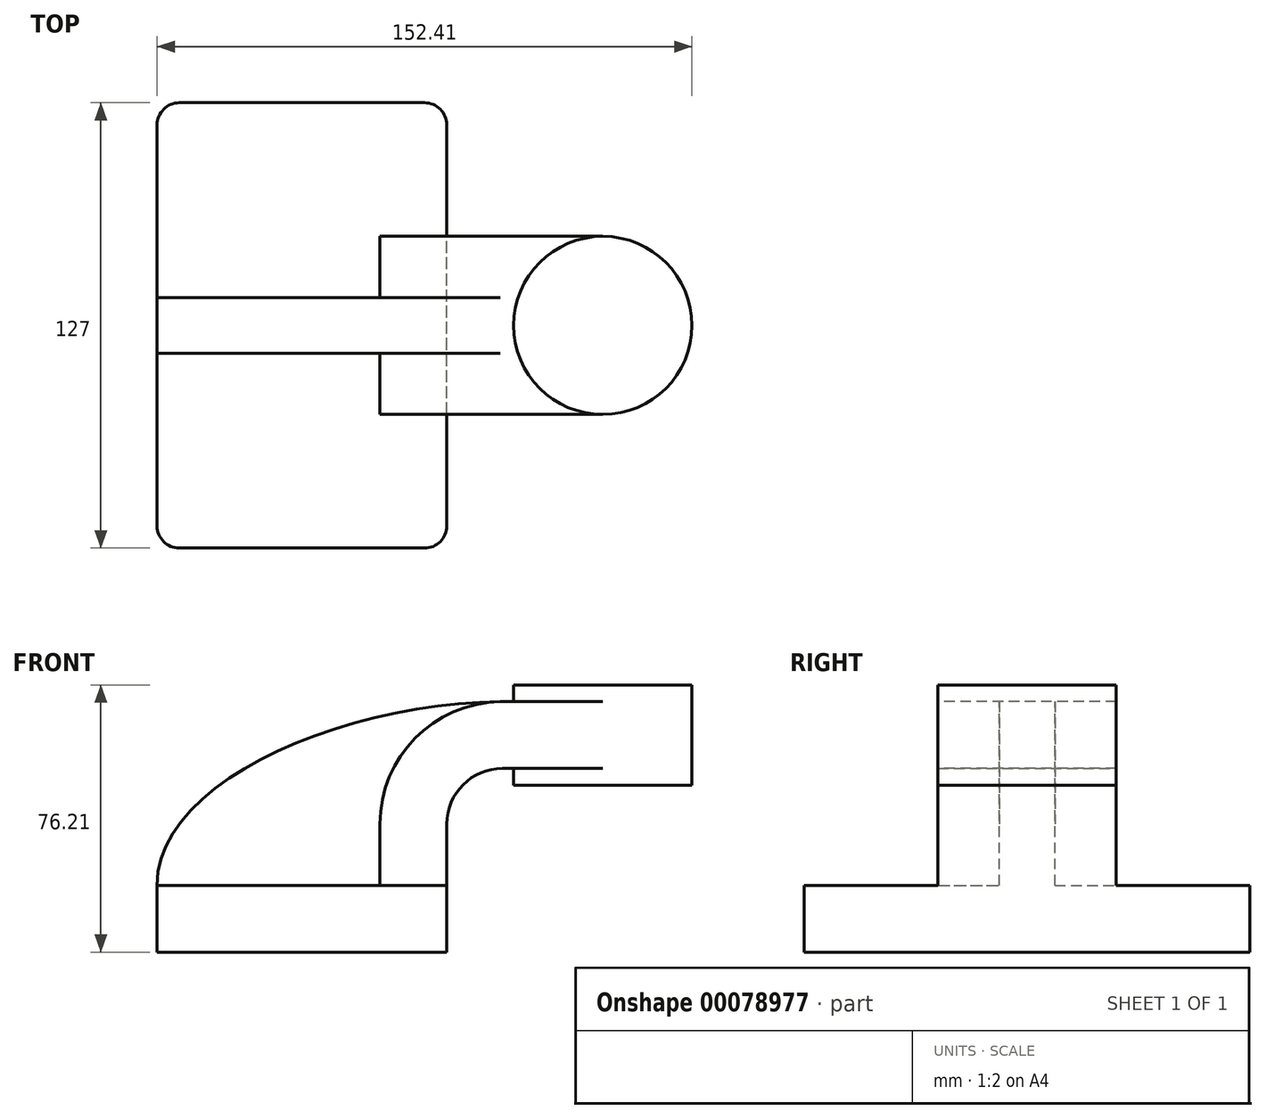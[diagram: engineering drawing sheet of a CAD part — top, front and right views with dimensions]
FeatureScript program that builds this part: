
annotation { "Feature Type Name" : "Feature", "Feature Type Description" : "" }
export const myFeature = defineFeature(function(context is Context, id is Id, definition is map)
    precondition{}
    {
        {
            var Q0;
            Q0=qCreatedBy(makeId("Front.planeOp"),FACE);
            var sketch = newSketch(context, id + "F0", { "sketchPlane" : qUnion([Q0])});
            skLineSegment(sketch, "E0.bottom", {"start": v(41.28, -9.53) * mm, "end": v(-41.27, -9.53) * mm});
            skLineSegment(sketch, "E0.top", {"start": v(41.28, 9.52) * mm, "end": v(-41.28, 9.52) * mm});
            skLineSegment(sketch, "E0.left", {"start": v(41.28, -9.53) * mm, "end": v(41.27, 9.52) * mm});
            skLineSegment(sketch, "E0.right", {"start": v(-41.27, -9.53) * mm, "end": v(-41.28, 9.52) * mm});
            skPoint(sketch, "E0.middle", {"position": v(0, 0) * mm});
            skLineSegment(sketch, "E1.bottom", {"start": v(111.12, 38.1) * mm, "end": v(60.33, 38.1) * mm});
            skLineSegment(sketch, "E1.top", {"start": v(111.12, 66.67) * mm, "end": v(60.33, 66.67) * mm});
            skLineSegment(sketch, "E1.left", {"start": v(111.12, 38.1) * mm, "end": v(111.12, 66.68) * mm});
            skLineSegment(sketch, "E1.right", {"start": v(60.33, 38.1) * mm, "end": v(60.33, 66.67) * mm});
            skPoint(sketch, "E1.middle", {"position": v(85.72, 52.39) * mm});
            skLineSegment(sketch, "E2", {"start": v(41.28, 9.52) * mm, "end": v(41.27, 26.99) * mm});
            skArc(sketch, "E3", {"start": v(41.27, 26.99) * mm, "mid": v(45.92, 38.21) * mm, "end": v(57.15, 42.86) * mm});
            skLineSegment(sketch, "E4", {"start": v(57.15, 42.86) * mm, "end": v(85.72, 42.86) * mm});
            skLineSegment(sketch, "E5.0", {"start": v(57.15, 61.91) * mm, "end": v(85.72, 61.91) * mm});
            skArc(sketch, "E5.1", {"start": v(22.22, 26.99) * mm, "mid": v(32.45, 51.68) * mm, "end": v(57.15, 61.91) * mm});
            skLineSegment(sketch, "E5.2", {"start": v(22.22, 9.52) * mm, "end": v(22.22, 26.99) * mm});
            skFitSpline(sketch, "E6", {"points": [v(-41.28, 9.52) * mm, v(57.15, 61.91) * mm], "startDerivative": vector(-0.62, 89.26) * mm, "endDerivative": vector(135.37, 0.89) * mm});
            skLineSegment(sketch, "E7", {"start": v(85.72, 66.68) * mm, "end": v(85.72, 38.1) * mm});
            skSolve(sketch);
        }
        {
            var Q0;
            Q0=makeQuery(id+"F0.imprint","IMPRINT",FACE,{"disambiguationData":[TD([[makeQuery(id+"F0.imprint","IMPRINT",EDGE,{"derivedFrom":sQuery(id+"F0.wireOp",EDGE,"E0.bottom")}),-1.0]])]});
            extrude(context, id + "F1", {"entities" : qUnion([Q0]), "endBound" : BoundingType.SYMMETRIC, "depth" : 127 * mm});
        }
        {
            var Q0;
            {var subQ1=sQuery(id+"F0.wireOp",EDGE,"E2");Q0=makeQuery(id+"F0.imprint","IMPRINT",FACE,{"disambiguationData":[TD([[makeQuery(id+"F0.imprint","IMPRINT",EDGE,{"derivedFrom":subQ1}),1.0]])]});}
            var Q1;
            {var subQ0=sQuery(id+"F0.wireOp",EDGE,"E4");var subQ1=sQuery(id+"F0.wireOp",EDGE,"E1.right");var subQ2=makeQuery(id+"F0.imprint","INTERSECT",VERTEX,{"derivedFrom":[subQ1,subQ0]});Q1=makeQuery(id+"F0.imprint","IMPRINT",FACE,{"disambiguationData":[TD([[makeQuery(id+"F0.imprint","IMPRINT",EDGE,{"disambiguationData":[TD([[subQ2,-1.0]])],"derivedFrom":subQ1}),-1.0]])]});}
            extrude(context, id + "F2", {"entities" : qUnion([Q0, Q1]), "operationType" : NewBodyOperationType.ADD, "endBound" : BoundingType.SYMMETRIC, "depth" : 50.8 * mm});
        }
        {
            var Q0;
            {var subQ3=sQuery(id+"F0.wireOp",EDGE,"E5.2");Q0=makeQuery(id+"F0.imprint","IMPRINT",FACE,{"disambiguationData":[TD([[makeQuery(id+"F0.imprint","IMPRINT",EDGE,{"derivedFrom":subQ3}),1.0]])]});}
            extrude(context, id + "F3", {"entities" : qUnion([Q0]), "operationType" : NewBodyOperationType.ADD, "endBound" : BoundingType.SYMMETRIC, "depth" : 15.88 * mm});
        }
        {
            var Q0;
            {var subQ4=sQuery(id+"F0.wireOp",EDGE,"E1.left");Q0=makeQuery(id+"F0.imprint","IMPRINT",FACE,{"disambiguationData":[TD([[makeQuery(id+"F0.imprint","IMPRINT",EDGE,{"derivedFrom":subQ4}),1.0]])]});}
            var Q1;
            Q1=sQuery(id+"F0.wireOp",EDGE,"E7");
            revolve(context, id + "F4", {"operationType" : NewBodyOperationType.ADD, "entities" : qUnion([Q0]), "axis" : qUnion([Q1]), "revolveType" : RevolveType.FULL});
        }
        {
            var Q0;
            Q0=makeQuery(id+"F1.opExtrude","CAP_EDGE",EDGE,{"disambiguationData":[OSD([sQuery(id+"F0.wireOp",EDGE,"E0.right")])],"isStart":false});
            var Q1;
            Q1=makeQuery(id+"F1.opExtrude","CAP_EDGE",EDGE,{"disambiguationData":[OSD([sQuery(id+"F0.wireOp",EDGE,"E0.left")])],"isStart":false});
            var Q2;
            Q2=makeQuery(id+"F1.opExtrude","CAP_EDGE",EDGE,{"disambiguationData":[OSD([sQuery(id+"F0.wireOp",EDGE,"E0.left")])],"isStart":true});
            var Q3;
            Q3=makeQuery(id+"F1.opExtrude","CAP_EDGE",EDGE,{"disambiguationData":[OSD([sQuery(id+"F0.wireOp",EDGE,"E0.right")])],"isStart":true});
            fillet(context, id + "F5", {"entities" : qUnion([Q0, Q1, Q2, Q3]), "radius" : 6.35 * mm, "tangentPropagation" : true, "allowEdgeOverflow" : false});
        }
    });
